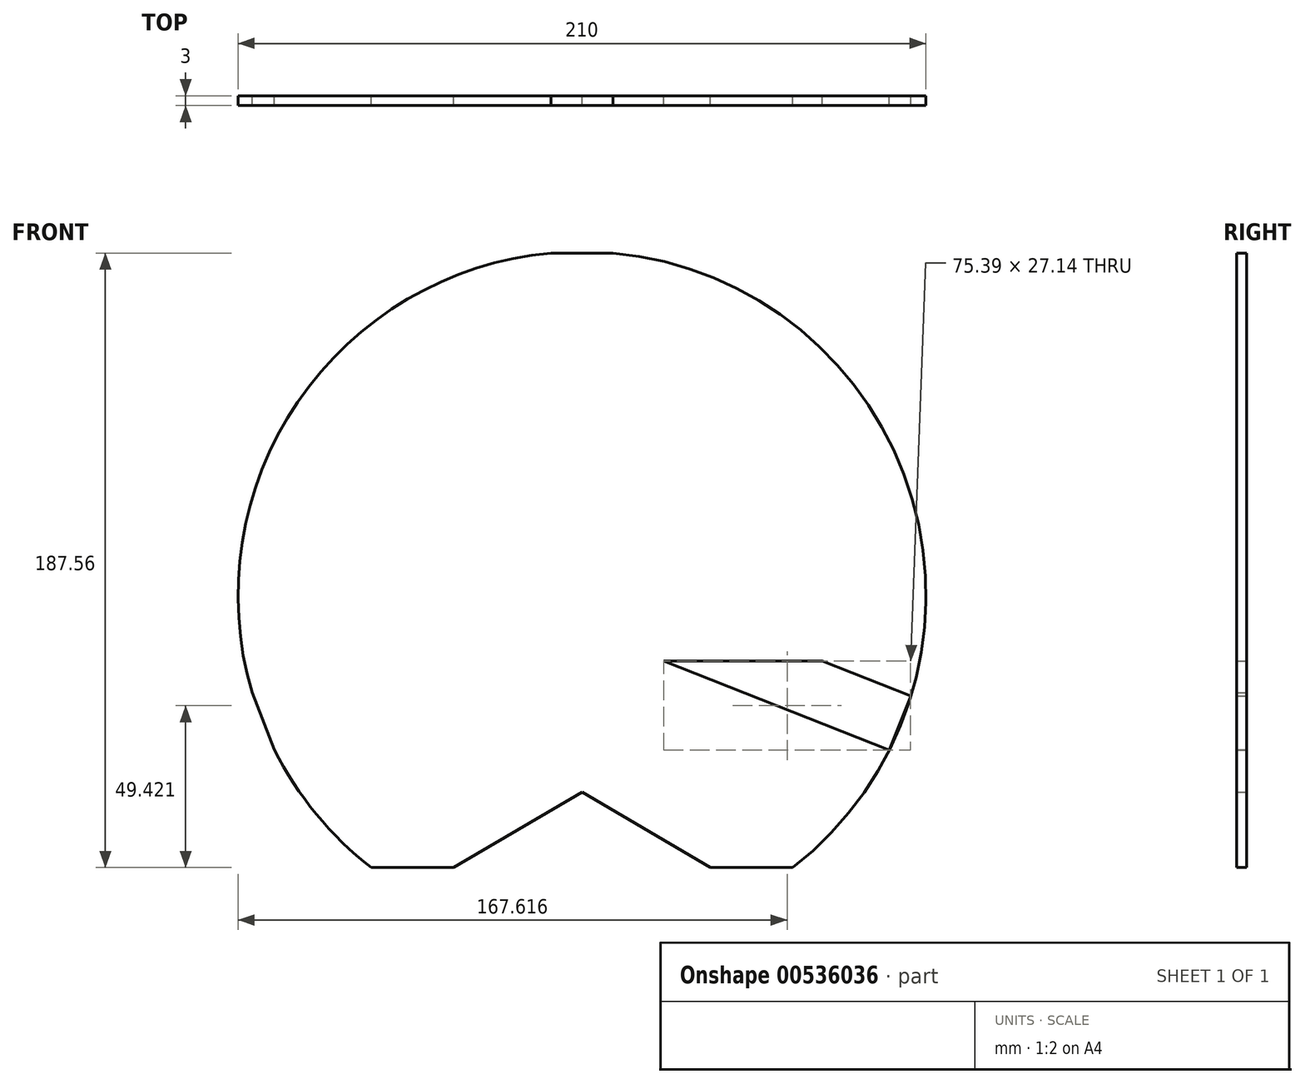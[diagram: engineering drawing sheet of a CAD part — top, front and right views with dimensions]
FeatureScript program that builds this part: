
annotation { "Feature Type Name" : "Feature", "Feature Type Description" : "" }
export const myFeature = defineFeature(function(context is Context, id is Id, definition is map)
    precondition{}
    {
        {
            var Q0;
            Q0=qCreatedBy(makeId("Front.planeOp"),FACE);
            var sketch = newSketch(context, id + "F0", { "sketchPlane" : qUnion([Q0])});
            skCircle(sketch, "E0", {"center": v(-16.98, 38.35) * mm, "radius": 105 * mm});
            skLineSegment(sketch, "E1", {"start": v(-16.98, 38.35) * mm, "end": v(-16.98, 143.35) * mm});
            skLineSegment(sketch, "E2", {"start": v(-16.98, 38.35) * mm, "end": v(-16.98, 18.35) * mm});
            skLineSegment(sketch, "E3", {"start": v(-16.98, 18.35) * mm, "end": v(86.1, 18.35) * mm});
            skLineSegment(sketch, "E4", {"start": v(-16.98, 18.35) * mm, "end": v(-120.06, 18.35) * mm});
            skLineSegment(sketch, "E5", {"start": v(-16.98, -21.65) * mm, "end": v(-69.6, -52.52) * mm});
            skLineSegment(sketch, "E6", {"start": v(35.63, -52.52) * mm, "end": v(-16.98, -21.65) * mm});
            skLineSegment(sketch, "E7", {"start": v(-81.3, -44.64) * mm, "end": v(-56.18, -44.64) * mm});
            skLineSegment(sketch, "E8", {"start": v(22.21, -44.64) * mm, "end": v(47.33, -44.64) * mm});
            skCircle(sketch, "E9.0", {"center": v(-16.98, 38.35) * mm, "radius": 111.35 * mm});
            skLineSegment(sketch, "E10", {"start": v(-103.15, -21.65) * mm, "end": v(-16.98, 18.35) * mm});
            skLineSegment(sketch, "E11", {"start": v(-16.98, 18.35) * mm, "end": v(69.18, -21.65) * mm});
            skLineSegment(sketch, "E12.bottom", {"start": v(-26.46, 142.92) * mm, "end": v(-7.51, 142.92) * mm});
            skLineSegment(sketch, "E12.top", {"start": v(-26.46, 46.92) * mm, "end": v(-7.51, 46.92) * mm});
            skLineSegment(sketch, "E12.left", {"start": v(-26.46, 142.92) * mm, "end": v(-26.46, 46.92) * mm});
            skLineSegment(sketch, "E12.right", {"start": v(-7.51, 142.92) * mm, "end": v(-7.51, 46.92) * mm});
            skLineSegment(sketch, "E13", {"start": v(80.3, 0.02) * mm, "end": v(83.33, 7.73) * mm});
            skLineSegment(sketch, "E14", {"start": v(-114.3, 0.01) * mm, "end": v(-117.76, 8.83) * mm});
            skLineSegment(sketch, "E15", {"start": v(-114.3, 0.01) * mm, "end": v(-110.83, -8.77) * mm});
            skLineSegment(sketch, "E16", {"start": v(80.3, 0.02) * mm, "end": v(76.83, -8.79) * mm});
            skLineSegment(sketch, "E17", {"start": v(-117.76, 8.83) * mm, "end": v(-110.83, -8.77) * mm});
            skLineSegment(sketch, "E18", {"start": v(83.33, 7.73) * mm, "end": v(76.83, -8.79) * mm});
            skLineSegment(sketch, "E19", {"start": v(-117.76, 8.83) * mm, "end": v(-28.44, 44.02) * mm});
            skLineSegment(sketch, "E20", {"start": v(-28.44, 44.02) * mm, "end": v(-25.36, 35.05) * mm});
            skLineSegment(sketch, "E21", {"start": v(-110.83, -8.77) * mm, "end": v(-21.51, 26.42) * mm});
            skPoint(sketch, "E21.endSnap0", {"position": v(-73.1, 26.42) * mm});
            skLineSegment(sketch, "E22", {"start": v(-25.36, 35.05) * mm, "end": v(-21.51, 26.42) * mm});
            skLineSegment(sketch, "E23", {"start": v(76.83, -8.79) * mm, "end": v(-12.5, 26.4) * mm});
            skLineSegment(sketch, "E24", {"start": v(-12.5, 26.4) * mm, "end": v(-8.61, 35.05) * mm});
            skLineSegment(sketch, "E25", {"start": v(83.33, 7.73) * mm, "end": v(-5.99, 42.92) * mm});
            skLineSegment(sketch, "E26", {"start": v(-5.99, 42.92) * mm, "end": v(-8.61, 35.05) * mm});
            skLineSegment(sketch, "E27.bottom", {"start": v(58.31, 41.78) * mm, "end": v(18.31, 41.78) * mm});
            skLineSegment(sketch, "E27.top", {"start": v(58.31, 81.78) * mm, "end": v(18.31, 81.78) * mm});
            skLineSegment(sketch, "E27.left", {"start": v(58.31, 41.78) * mm, "end": v(58.31, 81.78) * mm});
            skLineSegment(sketch, "E27.right", {"start": v(18.31, 41.78) * mm, "end": v(18.31, 81.78) * mm});
            skPoint(sketch, "E27.middle", {"position": v(38.31, 61.78) * mm});
            skPoint(sketch, "E28.middle", {"position": v(-72.28, 61.78) * mm});
            skLineSegment(sketch, "E29.bottom", {"start": v(-92.28, 81.78) * mm, "end": v(-52.28, 81.78) * mm});
            skLineSegment(sketch, "E29.top", {"start": v(-92.28, 41.78) * mm, "end": v(-52.28, 41.78) * mm});
            skLineSegment(sketch, "E29.left", {"start": v(-92.28, 81.78) * mm, "end": v(-92.28, 41.78) * mm});
            skLineSegment(sketch, "E29.right", {"start": v(-52.28, 81.78) * mm, "end": v(-52.28, 41.78) * mm});
            skSolve(sketch);
        }
        {
            var Q0;
            {var subQ3=sQuery(id+"F0.wireOp",EDGE,"E7");Q0=makeQuery(id+"F0.imprint","IMPRINT",FACE,{"disambiguationData":[TD([[makeQuery(id+"F0.imprint","IMPRINT",EDGE,{"derivedFrom":subQ3}),1.0]])]});}
            var Q1;
            {var subQ0=sQuery(id+"F0.wireOp",EDGE,"E10");Q1=makeQuery(id+"F0.imprint","IMPRINT",FACE,{"disambiguationData":[TD([[makeQuery(id+"F0.imprint","IMPRINT",EDGE,{"derivedFrom":subQ0}),1.0]])]});}
            var Q2;
            {var subQ4=sQuery(id+"F0.wireOp",EDGE,"E20");Q2=makeQuery(id+"F0.imprint","IMPRINT",FACE,{"disambiguationData":[TD([[makeQuery(id+"F0.imprint","IMPRINT",EDGE,{"derivedFrom":subQ4}),-1.0]])]});}
            var Q3;
            {var subQ3=sQuery(id+"F0.wireOp",EDGE,"E19");var subQ5=sQuery(id+"F0.wireOp",EDGE,"E0");var subQ6=makeQuery(id+"F0.imprint","INTERSECT",VERTEX,{"derivedFrom":[subQ5,subQ3]});Q3=makeQuery(id+"F0.imprint","IMPRINT",FACE,{"disambiguationData":[TD([[makeQuery(id+"F0.imprint","IMPRINT",EDGE,{"disambiguationData":[TD([[subQ6,-1.0]])],"derivedFrom":subQ5}),1.0]])]});}
            var Q4;
            {var subQ5=sQuery(id+"F0.wireOp",EDGE,"E2");Q4=makeQuery(id+"F0.imprint","IMPRINT",FACE,{"disambiguationData":[TD([[makeQuery(id+"F0.imprint","IMPRINT",EDGE,{"derivedFrom":subQ5}),-1.0]])]});}
            var Q5;
            {var subQ13=sQuery(id+"F0.wireOp",EDGE,"E2");Q5=makeQuery(id+"F0.imprint","IMPRINT",FACE,{"disambiguationData":[TD([[makeQuery(id+"F0.imprint","IMPRINT",EDGE,{"derivedFrom":subQ13}),1.0]])]});}
            var Q6;
            Q6=makeQuery(id+"F0.imprint","IMPRINT",FACE,{"disambiguationData":[TD([[makeQuery(id+"F0.imprint","IMPRINT",EDGE,{"derivedFrom":sQuery(id+"F0.wireOp",EDGE,"E27.bottom")}),-1.0]])]});
            var Q7;
            Q7=makeQuery(id+"F0.imprint","IMPRINT",FACE,{"disambiguationData":[TD([[makeQuery(id+"F0.imprint","IMPRINT",EDGE,{"derivedFrom":sQuery(id+"F0.wireOp",EDGE,"E29.bottom")}),-1.0]])]});
            var Q8;
            {var subQ5=sQuery(id+"F0.wireOp",EDGE,"E12.left");Q8=makeQuery(id+"F0.imprint","IMPRINT",FACE,{"disambiguationData":[TD([[makeQuery(id+"F0.imprint","IMPRINT",EDGE,{"derivedFrom":subQ5}),1.0]])]});}
            var Q9;
            {var subQ5=sQuery(id+"F0.wireOp",EDGE,"E12.right");Q9=makeQuery(id+"F0.imprint","IMPRINT",FACE,{"disambiguationData":[TD([[makeQuery(id+"F0.imprint","IMPRINT",EDGE,{"derivedFrom":subQ5}),-1.0]])]});}
            var Q10;
            {var subQ4=sQuery(id+"F0.wireOp",EDGE,"E24");Q10=makeQuery(id+"F0.imprint","IMPRINT",FACE,{"disambiguationData":[TD([[makeQuery(id+"F0.imprint","IMPRINT",EDGE,{"derivedFrom":subQ4}),-1.0]])]});}
            var Q11;
            {var subQ5=sQuery(id+"F0.wireOp",EDGE,"E18");Q11=makeQuery(id+"F0.imprint","IMPRINT",FACE,{"disambiguationData":[TD([[makeQuery(id+"F0.imprint","IMPRINT",EDGE,{"derivedFrom":subQ5}),-1.0]])]});}
            var Q12;
            {var subQ6=sQuery(id+"F0.wireOp",EDGE,"E11");Q12=makeQuery(id+"F0.imprint","IMPRINT",FACE,{"disambiguationData":[TD([[makeQuery(id+"F0.imprint","IMPRINT",EDGE,{"derivedFrom":subQ6}),1.0]])]});}
            var Q13;
            {var subQ0=sQuery(id+"F0.wireOp",EDGE,"E4");var subQ1=sQuery(id+"F0.wireOp",EDGE,"E0");var subQ2=makeQuery(id+"F0.imprint","INTERSECT",VERTEX,{"derivedFrom":[subQ1,subQ0]});Q13=makeQuery(id+"F0.imprint","IMPRINT",FACE,{"disambiguationData":[TD([[makeQuery(id+"F0.imprint","IMPRINT",EDGE,{"disambiguationData":[TD([[subQ2,-1.0]])],"derivedFrom":subQ1}),1.0]])]});}
            extrude(context, id + "F1", {"entities" : qUnion([Q0, Q1, Q2, Q3, Q4, Q5, Q6, Q7, Q8, Q9, Q10, Q11, Q12, Q13]), "depth" : 3 * mm, "offsetDistance" : 25.4 * mm});
        }
    });
